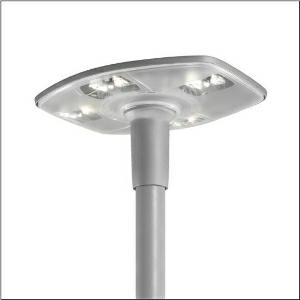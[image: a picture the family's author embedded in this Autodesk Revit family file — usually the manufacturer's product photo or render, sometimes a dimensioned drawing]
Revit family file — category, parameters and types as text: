
# Revit family: dl_30_led___st1_2c_5xa513281b08a5_8ddb
name_source: partatom
category: Lighting Fixtures
units: mm (PartAtom-declared; Revit-internal decimal feet)

## family parameters
Cut with Voids When Loaded = No
Host = Face
Light Source = No
Part Type = Normal
Room Calculation Point = No
Round Connector Dimension = Use Diameter
Shared = No

## types (1)
- --- (1 x LED, 4590 lm, 49 W, 3000K)
    Apparent Load = 49 VA
    CIE Flux Codes = 32 71 98 100 100
    Color Rendering = 80
    Color Temperature = 3000K
    Default Elevation = 1800 mm
    Description = DL 30 LED, mast luminaire, primary light control with 3 zone facetted reflector, of plastic, aluminium vaporised, highly specular, primary optical cover: cover, of PMMA, structured, transparent, light distribution: ST1.2c, light emission: direct distribution, primary light characteristic: asymmetric, crossroads, installation type: post-top, LED, High Power LED, rated luminous flux: 4.590lm, luminous efficacy: 94lm/W, light colour: 830, colour temperature: 3000K, control gear: Plus, control: flexible luminous flux parameterisation, time-dependent luminous flux control, constant luminous flux control, digital communication interface, power reduction, electronic power reduction, mains connection: 230..240V, AC, 50/60Hz, start of lifetime: 49W, end of service life: 51W, reduction: 22W, luminaire housing, of diecast aluminium, powder-coated, SITECO metallic grey (DB 702S), length: 600mm, width: 510mm, height: 290mm, spigot size: d x l = 76 x 100mm (post-top) | with reducer (optional accessory) 60 x 100mm, mounting height: 3..6m, protection rating (complete): IP66, insulation class (complete): insulation class II (safety insulation), certification: CE, ENEC, VDE, impact resistance: IK08, permissible operating ambient temperature: -25..+30°C, standard-compliant lighting for roads and squares, packaging unit: 1 piece

Light Distribution: ST1.2c
    Height = 290 mm
    Lamp = 1 x LED
    Lamp Light Flux = 4590 lm
    Lamp Power = 49 W
    Lamp count = 1
    Length = 510 mm
    Luminous efficacy = 94 lm/W
    Manufacturer = Siteco
    ModVariant = No
    Model = 5XA513281B08A5
    Number of Poles = 1
    OnlyDefault = Yes
    Power Factor = 1
    Product Name = DL 30 LED | ST1.2c
    Product group = mast luminaire | pylon top
    ProductGroupID = 6100
    Protection Class = Protection class II
    Protection Degree = IP 66
    RLX_Detail_Level = 1
    RLX_Emergency_Light_Flux = 0 lm
    RLX_Emergency_Type = 0
    RLX_Emergency_Type_DB = No
    RlxData = <blob elided: 86441 chars, md5=d27053cb>
    Socket = socket
    Standby Power = 0 W
    System Light Flux = 4590 lm
    System Power = 49 W
    Type Comments = factory setting: luminous flux: 100 % | dim-lin: 254 | 497 mA
    Type Image = l_1006003.jpg
    URL = http://relux.com
    VarID = @adj_195393
    Voltage = 0 V
    Weight = 0.00 kg
    Width = 600 mm

## geometry (parser evidence)
native form markers: Blend x4, Sweep x13
no freeform markers — native parametric forms only
